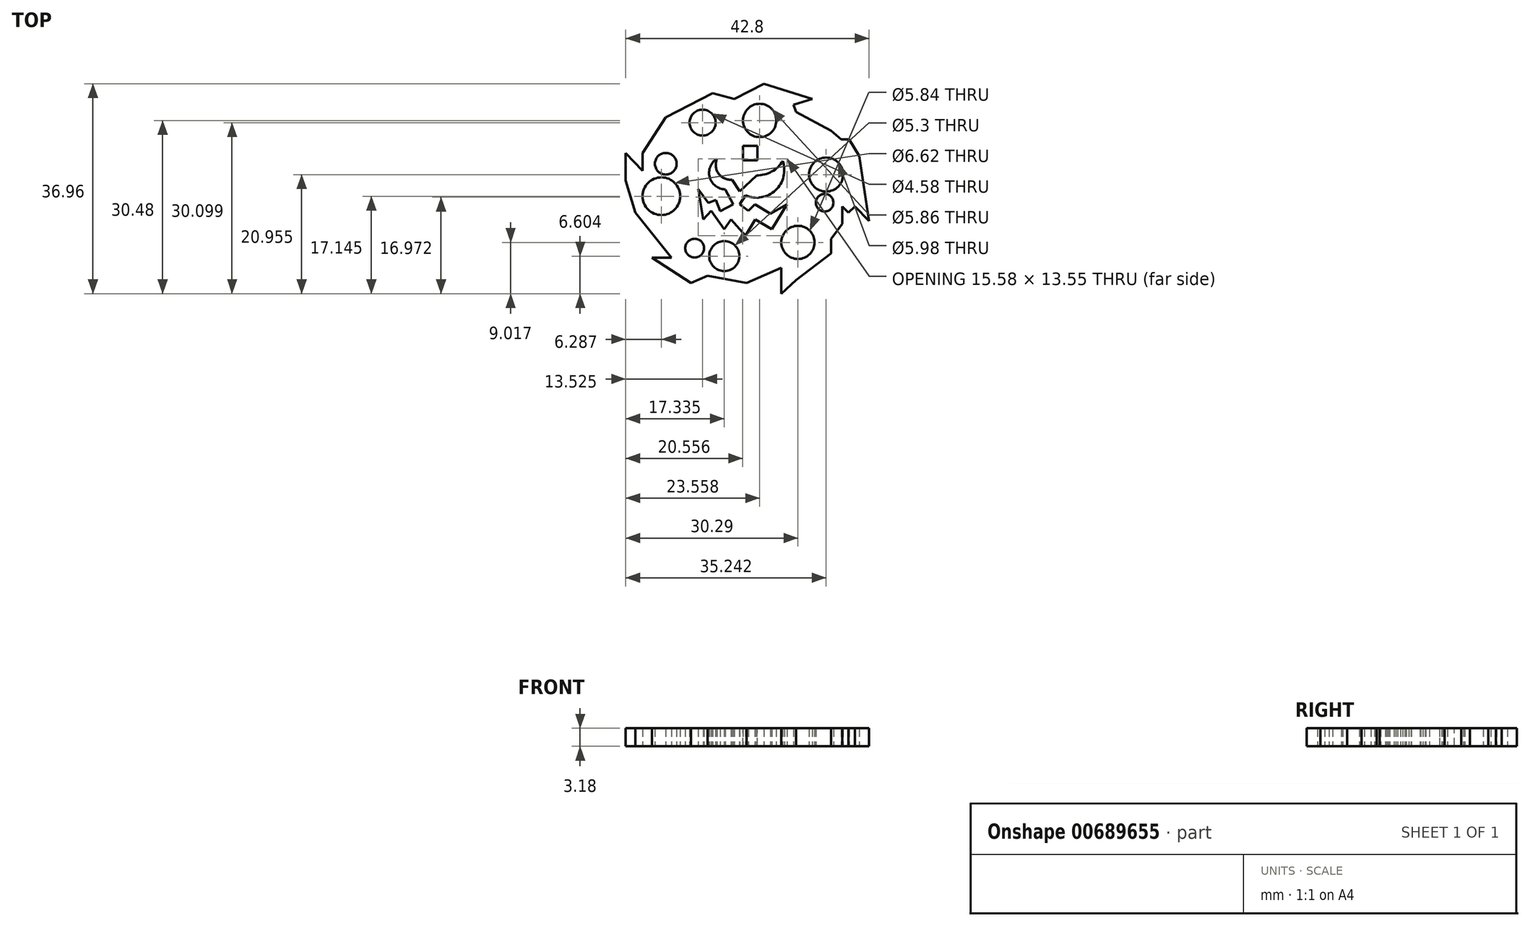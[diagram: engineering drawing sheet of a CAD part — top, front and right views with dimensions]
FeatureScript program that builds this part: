
annotation { "Feature Type Name" : "Feature", "Feature Type Description" : "" }
export const myFeature = defineFeature(function(context is Context, id is Id, definition is map)
    precondition{}
    {
        {
            var Q0;
            Q0=qCreatedBy(makeId("Top.planeOp"),FACE);
            var sketch = newSketch(context, id + "F0", { "sketchPlane" : qUnion([Q0])});
            skLineSegment(sketch, "E0", {"start": v(24.32, -0.95) * mm, "end": v(32.83, -3.62) * mm});
            skLineSegment(sketch, "E1", {"start": v(32.83, -3.62) * mm, "end": v(29.53, -4.64) * mm});
            skLineSegment(sketch, "E2", {"start": v(29.53, -4.64) * mm, "end": v(29.94, -5.97) * mm});
            skLineSegment(sketch, "E3", {"start": v(29.94, -5.97) * mm, "end": v(36.13, -9.2) * mm});
            skLineSegment(sketch, "E4", {"start": v(36.13, -9.2) * mm, "end": v(37.9, -10.73) * mm});
            skLineSegment(sketch, "E5", {"start": v(37.9, -10.73) * mm, "end": v(39.3, -10.73) * mm});
            skLineSegment(sketch, "E6", {"start": v(39.3, -10.73) * mm, "end": v(41.08, -13.65) * mm});
            skLineSegment(sketch, "E7", {"start": v(41.08, -13.65) * mm, "end": v(42.8, -25.08) * mm});
            skLineSegment(sketch, "E8", {"start": v(42.8, -25.08) * mm, "end": v(40.32, -22.54) * mm});
            skLineSegment(sketch, "E9", {"start": v(40.32, -22.54) * mm, "end": v(39.17, -23.67) * mm});
            skLineSegment(sketch, "E10", {"start": v(39.17, -23.67) * mm, "end": v(38.07, -22.54) * mm});
            skLineSegment(sketch, "E11", {"start": v(38.07, -22.54) * mm, "end": v(38.07, -25.6) * mm});
            skLineSegment(sketch, "E12", {"start": v(38.07, -25.6) * mm, "end": v(36.13, -28.26) * mm});
            skLineSegment(sketch, "E13", {"start": v(36.13, -28.26) * mm, "end": v(36.13, -30.8) * mm});
            skLineSegment(sketch, "E14", {"start": v(36.13, -30.8) * mm, "end": v(29.94, -35.5) * mm});
            skLineSegment(sketch, "E15", {"start": v(29.94, -35.5) * mm, "end": v(27.37, -37.9) * mm});
            skLineSegment(sketch, "E16", {"start": v(27.37, -37.9) * mm, "end": v(27.37, -33.34) * mm});
            skLineSegment(sketch, "E17", {"start": v(27.37, -33.34) * mm, "end": v(21.27, -36) * mm});
            skLineSegment(sketch, "E18", {"start": v(21.27, -36) * mm, "end": v(14.41, -34.73) * mm});
            skLineSegment(sketch, "E19", {"start": v(14.41, -34.73) * mm, "end": v(11.5, -36) * mm});
            skLineSegment(sketch, "E20", {"start": v(11.5, -36) * mm, "end": v(4.64, -31.56) * mm});
            skLineSegment(sketch, "E21", {"start": v(4.64, -31.56) * mm, "end": v(8.06, -31.56) * mm});
            skLineSegment(sketch, "E22", {"start": v(8.06, -31.56) * mm, "end": v(1.71, -23.67) * mm});
            skLineSegment(sketch, "E23", {"start": v(1.71, -23.67) * mm, "end": v(0, -17.97) * mm});
            skLineSegment(sketch, "E24", {"start": v(0, -17.97) * mm, "end": v(0, -13.14) * mm});
            skLineSegment(sketch, "E25", {"start": v(0, -13.14) * mm, "end": v(2.98, -16.31) * mm});
            skLineSegment(sketch, "E26", {"start": v(2.98, -16.31) * mm, "end": v(2.98, -13.14) * mm});
            skLineSegment(sketch, "E27", {"start": v(2.98, -13.14) * mm, "end": v(7.04, -6.87) * mm});
            skLineSegment(sketch, "E28", {"start": v(7.04, -6.87) * mm, "end": v(15.3, -2.6) * mm});
            skLineSegment(sketch, "E29", {"start": v(15.3, -2.6) * mm, "end": v(19.11, -3.62) * mm});
            skLineSegment(sketch, "E30", {"start": v(19.11, -3.62) * mm, "end": v(24.32, -0.95) * mm});
            skCircle(sketch, "E31", {"center": v(23.56, -7.43) * mm, "radius": 2.93 * mm});
            skCircle(sketch, "E32", {"center": v(13.53, -7.81) * mm, "radius": 2.29 * mm});
            skCircle(sketch, "E33", {"center": v(7.05, -15.05) * mm, "radius": 1.9 * mm});
            skCircle(sketch, "E34", {"center": v(6.29, -20.76) * mm, "radius": 3.31 * mm});
            skCircle(sketch, "E35", {"center": v(12.13, -29.9) * mm, "radius": 1.66 * mm});
            skCircle(sketch, "E36", {"center": v(17.34, -31.3) * mm, "radius": 2.65 * mm});
            skCircle(sketch, "E37", {"center": v(30.29, -28.9) * mm, "radius": 2.92 * mm});
            skCircle(sketch, "E38", {"center": v(34.99, -21.9) * mm, "radius": 1.55 * mm});
            skCircle(sketch, "E39", {"center": v(35.24, -16.95) * mm, "radius": 2.99 * mm});
            skLineSegment(sketch, "E40", {"start": v(12.76, -19.5) * mm, "end": v(13.62, -24.86) * mm});
            skLineSegment(sketch, "E41", {"start": v(13.62, -24.86) * mm, "end": v(15.05, -23.3) * mm});
            skLineSegment(sketch, "E42", {"start": v(15.05, -23.3) * mm, "end": v(17.32, -26.6) * mm});
            skLineSegment(sketch, "E43", {"start": v(17.32, -26.6) * mm, "end": v(18.5, -24.86) * mm});
            skLineSegment(sketch, "E44", {"start": v(18.5, -24.86) * mm, "end": v(21.08, -27.71) * mm});
            skLineSegment(sketch, "E45", {"start": v(21.08, -27.71) * mm, "end": v(22.8, -24.86) * mm});
            skLineSegment(sketch, "E46", {"start": v(22.8, -24.86) * mm, "end": v(25.7, -26.6) * mm});
            skLineSegment(sketch, "E47", {"start": v(25.7, -26.6) * mm, "end": v(28.35, -22.2) * mm});
            skLineSegment(sketch, "E48", {"start": v(28.35, -22.2) * mm, "end": v(25.42, -23.8) * mm});
            skLineSegment(sketch, "E49", {"start": v(25.42, -23.8) * mm, "end": v(22.7, -22.2) * mm});
            skLineSegment(sketch, "E50", {"start": v(22.7, -22.2) * mm, "end": v(21.6, -23.3) * mm});
            skLineSegment(sketch, "E51", {"start": v(21.6, -23.3) * mm, "end": v(20.07, -22.2) * mm});
            skLineSegment(sketch, "E52", {"start": v(20.07, -22.2) * mm, "end": v(21.08, -20.62) * mm});
            skLineSegment(sketch, "E53", {"start": v(12.76, -19.5) * mm, "end": v(14.54, -21.9) * mm});
            skLineSegment(sketch, "E54", {"start": v(14.54, -21.9) * mm, "end": v(15.83, -21.4) * mm});
            skPoint(sketch, "E54.endSnap0", {"position": v(42.8, -21.4) * mm});
            skLineSegment(sketch, "E55", {"start": v(15.83, -21.4) * mm, "end": v(16.61, -23.39) * mm});
            skLineSegment(sketch, "E56", {"start": v(16.61, -23.39) * mm, "end": v(18.88, -22.2) * mm});
            skLineSegment(sketch, "E57", {"start": v(18.88, -22.2) * mm, "end": v(17.5, -19.56) * mm});
            skArc(sketch, "E58", {"start": v(16.07, -14.16) * mm, "mid": v(14.76, -17.4) * mm, "end": v(17.5, -19.56) * mm});
            skArc(sketch, "E59", {"start": v(16.07, -14.16) * mm, "mid": v(16.33, -16.78) * mm, "end": v(18.73, -17.84) * mm});
            skArc(sketch, "E60", {"start": v(21.08, -20.62) * mm, "mid": v(26.34, -19.72) * mm, "end": v(27.62, -14.54) * mm});
            skArc(sketch, "E61", {"start": v(23.02, -17.08) * mm, "mid": v(25.67, -16.44) * mm, "end": v(27.62, -14.54) * mm});
            skLineSegment(sketch, "E62", {"start": v(18.73, -17.84) * mm, "end": v(20.07, -19.91) * mm});
            skLineSegment(sketch, "E63", {"start": v(23.02, -17.08) * mm, "end": v(20.07, -19.91) * mm});
            skSolve(sketch);
        }
        {
            var Q0;
            Q0=makeQuery(id+"F0.imprint","IMPRINT",FACE,{"disambiguationData":[TD([[makeQuery(id+"F0.imprint","IMPRINT",EDGE,{"derivedFrom":sQuery(id+"F0.wireOp",EDGE,"E0")}),-1.0]])]});
            extrude(context, id + "F1", {"entities" : qUnion([Q0]), "depth" : 3.17 * mm, "offsetDistance" : 25.4 * mm});
        }
        {
            var Q0;
            Q0=makeQuery(id+"F1.opExtrude","CAP_FACE",FACE,{"disambiguationData":[OSD([sQuery(id+"F0.wireOp",EDGE,"E0"),sQuery(id+"F0.wireOp",EDGE,"E1"),sQuery(id+"F0.wireOp",EDGE,"E2"),sQuery(id+"F0.wireOp",EDGE,"E3"),sQuery(id+"F0.wireOp",EDGE,"E4"),sQuery(id+"F0.wireOp",EDGE,"E5"),sQuery(id+"F0.wireOp",EDGE,"E6"),sQuery(id+"F0.wireOp",EDGE,"E7"),sQuery(id+"F0.wireOp",EDGE,"E8"),sQuery(id+"F0.wireOp",EDGE,"E9"),sQuery(id+"F0.wireOp",EDGE,"E10"),sQuery(id+"F0.wireOp",EDGE,"E11"),sQuery(id+"F0.wireOp",EDGE,"E12"),sQuery(id+"F0.wireOp",EDGE,"E13"),sQuery(id+"F0.wireOp",EDGE,"E14"),sQuery(id+"F0.wireOp",EDGE,"E15"),sQuery(id+"F0.wireOp",EDGE,"E16"),sQuery(id+"F0.wireOp",EDGE,"E17"),sQuery(id+"F0.wireOp",EDGE,"E18"),sQuery(id+"F0.wireOp",EDGE,"E19"),sQuery(id+"F0.wireOp",EDGE,"E20"),sQuery(id+"F0.wireOp",EDGE,"E21"),sQuery(id+"F0.wireOp",EDGE,"E22"),sQuery(id+"F0.wireOp",EDGE,"E23"),sQuery(id+"F0.wireOp",EDGE,"E24"),sQuery(id+"F0.wireOp",EDGE,"E25"),sQuery(id+"F0.wireOp",EDGE,"E26"),sQuery(id+"F0.wireOp",EDGE,"E27"),sQuery(id+"F0.wireOp",EDGE,"E28"),sQuery(id+"F0.wireOp",EDGE,"E29"),sQuery(id+"F0.wireOp",EDGE,"E30"),sQuery(id+"F0.wireOp",EDGE,"E31"),sQuery(id+"F0.wireOp",EDGE,"E32"),sQuery(id+"F0.wireOp",EDGE,"tmOFHkj1-5isa-cLvi-yrdd-mBPDGIu0XdM1"),sQuery(id+"F0.wireOp",EDGE,"E33"),sQuery(id+"F0.wireOp",EDGE,"E34"),sQuery(id+"F0.wireOp",EDGE,"r9954BxS-MbYq-6Xdp-X3RM-8pOFGW7YhAuD"),sQuery(id+"F0.wireOp",EDGE,"E35"),sQuery(id+"F0.wireOp",EDGE,"E36"),sQuery(id+"F0.wireOp",EDGE,"sd1KIute-3zRj-OFJe-RDWO-xVAyN5kZJWR6"),sQuery(id+"F0.wireOp",EDGE,"E37"),sQuery(id+"F0.wireOp",EDGE,"QsxojUJz-8UD4-V7cv-eFAD-WeoUi0TcNC1u"),sQuery(id+"F0.wireOp",EDGE,"E38"),sQuery(id+"F0.wireOp",EDGE,"E39"),sQuery(id+"F0.wireOp",EDGE,"Rw1vG9PU-xXsp-CIhO-AWKe-ddtmglRLt4S2"),sQuery(id+"F0.wireOp",EDGE,"QE612ZpV-XVtv-zLmR-d1fK-00GWUMO0Wkld"),sQuery(id+"F0.wireOp",EDGE,"E40"),sQuery(id+"F0.wireOp",EDGE,"E41"),sQuery(id+"F0.wireOp",EDGE,"E42"),sQuery(id+"F0.wireOp",EDGE,"E43"),sQuery(id+"F0.wireOp",EDGE,"E44"),sQuery(id+"F0.wireOp",EDGE,"E45"),sQuery(id+"F0.wireOp",EDGE,"E46"),sQuery(id+"F0.wireOp",EDGE,"E47"),sQuery(id+"F0.wireOp",EDGE,"E48"),sQuery(id+"F0.wireOp",EDGE,"E49"),sQuery(id+"F0.wireOp",EDGE,"E50"),sQuery(id+"F0.wireOp",EDGE,"E51"),sQuery(id+"F0.wireOp",EDGE,"E52"),sQuery(id+"F0.wireOp",EDGE,"E53"),sQuery(id+"F0.wireOp",EDGE,"E54"),sQuery(id+"F0.wireOp",EDGE,"E55"),sQuery(id+"F0.wireOp",EDGE,"E56"),sQuery(id+"F0.wireOp",EDGE,"E57"),sQuery(id+"F0.wireOp",EDGE,"E58"),sQuery(id+"F0.wireOp",EDGE,"E59"),sQuery(id+"F0.wireOp",EDGE,"E60"),sQuery(id+"F0.wireOp",EDGE,"E61"),sQuery(id+"F0.wireOp",EDGE,"E62"),sQuery(id+"F0.wireOp",EDGE,"E63")])],"isStart":false});
            var sketch = newSketch(context, id + "F2", { "sketchPlane" : qUnion([Q0])});
            skLineSegment(sketch, "E64.bottom", {"start": v(23.17, -11.92) * mm, "end": v(20.63, -11.92) * mm});
            skLineSegment(sketch, "E64.top", {"start": v(23.17, -14.46) * mm, "end": v(20.63, -14.46) * mm});
            skLineSegment(sketch, "E64.left", {"start": v(23.17, -11.92) * mm, "end": v(23.17, -14.46) * mm});
            skLineSegment(sketch, "E64.right", {"start": v(20.63, -11.92) * mm, "end": v(20.63, -14.46) * mm});
            skSolve(sketch);
        }
        {
            var Q0;
            Q0=makeQuery(id+"F2.imprint","IMPRINT",FACE,{"disambiguationData":[TD([[makeQuery(id+"F2.imprint","IMPRINT",EDGE,{"derivedFrom":sQuery(id+"F2.wireOp",EDGE,"E64.bottom")}),1.0]])]});
            extrude(context, id + "F3", {"entities" : qUnion([Q0]), "operationType" : NewBodyOperationType.REMOVE, "oppositeDirection" : true, "depth" : 3.17 * mm, "offsetDistance" : 25.4 * mm});
        }
    });
